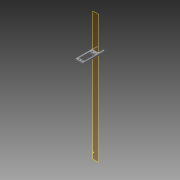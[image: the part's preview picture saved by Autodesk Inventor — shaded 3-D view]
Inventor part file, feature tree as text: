
AUTODESK INVENTOR PART (.ipt)
format: ipt  version: 2015 (Build 190159000, 159)  size: 160,768 bytes
history: native  units: in
note: dims shown in document units (in); Inventor stores cm internally (conversion verified against a paired STEP export)
features: reference x14, sketch x8, extrude x7, projected_geometry x3, plane x2
ambient origin geometry x8: Origin, YZ Plane, XZ Plane, XY Plane, X Axis, Y Axis, Z Axis, Center Point
bodies: Solid1 (feature_tree)
feature tree (34):
  plane  "Work Plane1"
  plane  "Work Plane2"
  extrude  "Extrusion1"  Depth=2.4375in TaperAngle=0.0deg
  extrude  "Extrusion2"  Depth=0.75in TaperAngle=0.0deg
  extrude  "Extrusion3"  TaperAngle=180.0deg  [1 undecoded]
  extrude  "Extrusion4"  Depth=0.5in
  extrude  "Extrusion5"  Depth=0.5in TaperAngle=0.0deg
  extrude  "Extrusion6"  [1 undecoded]
  sketch  "Sketch10"
  extrude  "Extrusion7"  [1 undecoded]
  sketch  "Sketch2"  dims[d0=2.4375in d1=0.0in d2=2.4375in d3=0.0in]
  reference  "Reference1"
  reference  "Reference2"
  sketch  "Sketch3"  dims[d4=2.4375in d5=0.0in d6=0.75in d7=0.0in]
  reference  "Reference3"
  reference  "Reference4"
  reference  "Reference5"
  reference  "Reference6"
  sketch  "Sketch4"  dims[d8=0.5625in d9=0.0in d10=180.0deg]
  reference  "Reference7"
  reference  "Reference8"
  reference  "Reference9"
  reference  "Reference10"
  sketch  "Sketch6"  dims[d11=0.5in d12=0.0in d13=0.1406in]
  projected_geometry  "Projected Loop1"
  sketch  "Sketch7"  dims[d14=0.1406in d15=0.5in d16=0.0in]
  reference  "Reference13"
  reference  "Reference14"
  reference  "Reference15"
  reference  "Reference16"
  sketch  "Sketch8"
  projected_geometry  "Projected Loop2"
  sketch  "Sketch11"
  projected_geometry  "Projected Loop3"
note: 3 required parameter values undecoded (feature->parameter linkage not recoverable at this tier; creation-order binding heuristic only, values carry confidence <= 0.55)
